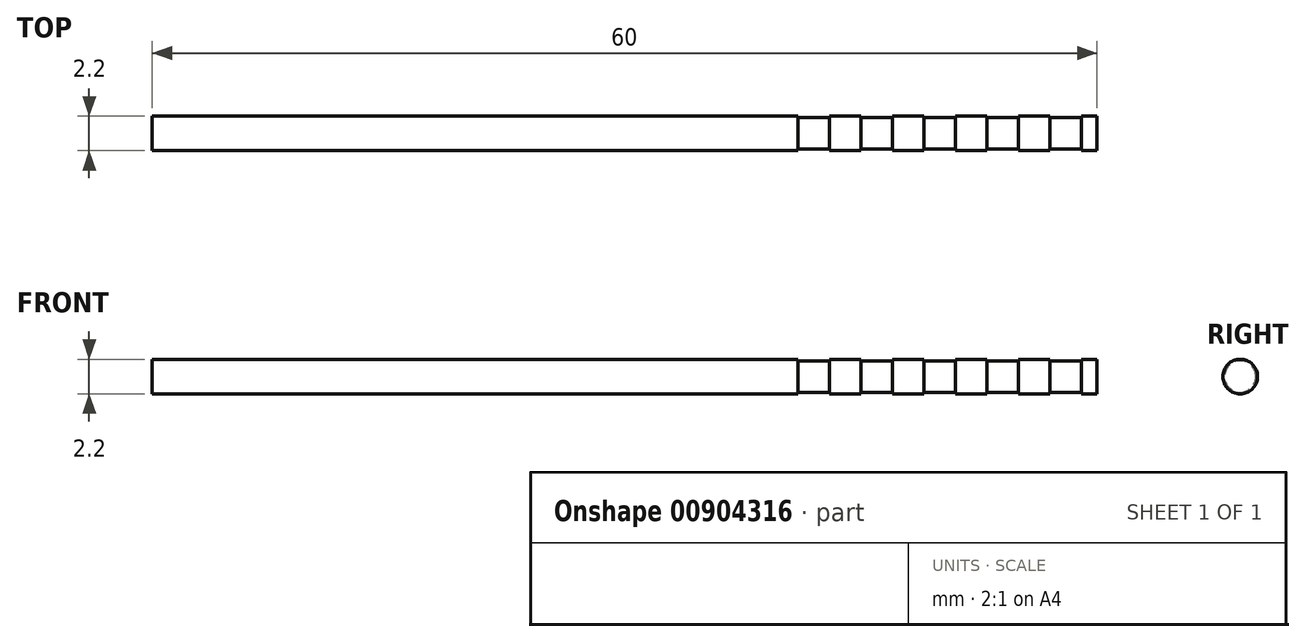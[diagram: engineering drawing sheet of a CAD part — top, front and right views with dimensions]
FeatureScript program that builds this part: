
annotation { "Feature Type Name" : "Feature", "Feature Type Description" : "" }
export const myFeature = defineFeature(function(context is Context, id is Id, definition is map)
    precondition{}
    {
        {
            var Q0;
            Q0=qCreatedBy(makeId("Front.planeOp"),FACE);
            var sketch = newSketch(context, id + "F0", { "sketchPlane" : qUnion([Q0])});
            skLineSegment(sketch, "E0.bottom", {"start": v(0, 0) * mm, "end": v(-25, 0) * mm});
            skLineSegment(sketch, "E0.top", {"start": v(0, 1.1) * mm, "end": v(-25, 1.1) * mm});
            skLineSegment(sketch, "E0.left", {"start": v(0, 0) * mm, "end": v(0, 1.1) * mm});
            skLineSegment(sketch, "E0.right", {"start": v(-25, 0) * mm, "end": v(-25, 1.1) * mm});
            skLineSegment(sketch, "E1.top", {"start": v(0, 1) * mm, "end": v(-25, 1) * mm});
            skLineSegment(sketch, "E1.left", {"start": v(0, 0) * mm, "end": v(0, 1) * mm});
            skLineSegment(sketch, "E1.right", {"start": v(-25, 0) * mm, "end": v(-25, 1) * mm});
            skLineSegment(sketch, "E2", {"start": v(-1, 1.1) * mm, "end": v(-1, 0) * mm});
            skLineSegment(sketch, "E3", {"start": v(-3, 1.1) * mm, "end": v(-3, 0) * mm});
            skLineSegment(sketch, "E4", {"start": v(-5, 1.1) * mm, "end": v(-5, 0) * mm});
            skLineSegment(sketch, "E5", {"start": v(-7, 1.1) * mm, "end": v(-7, 0) * mm});
            skLineSegment(sketch, "E6", {"start": v(-9, 1.1) * mm, "end": v(-9, 0) * mm});
            skLineSegment(sketch, "E7", {"start": v(-11, 1.1) * mm, "end": v(-11, 0) * mm});
            skLineSegment(sketch, "E8", {"start": v(-13, 1.1) * mm, "end": v(-13, 0) * mm});
            skLineSegment(sketch, "E9", {"start": v(-15, 1.1) * mm, "end": v(-15, 0) * mm});
            skLineSegment(sketch, "E10", {"start": v(-17, 1.1) * mm, "end": v(-17, 0) * mm});
            skLineSegment(sketch, "E11", {"start": v(-19, 1.1) * mm, "end": v(-19, 0) * mm});
            skSolve(sketch);
        }
        {
            var Q0;
            {var subQ0=sQuery(id+"F0.wireOp",EDGE,"E0.right");Q0=makeQuery(id+"F0.imprint","IMPRINT",FACE,{"disambiguationData":[TD([[makeQuery(id+"F0.imprint","IMPRINT",EDGE,{"derivedFrom":subQ0}),-1.0]])]});}
            var Q1;
            {var subQ0=sQuery(id+"F0.wireOp",EDGE,"E1.right");Q1=makeQuery(id+"F0.imprint","IMPRINT",FACE,{"disambiguationData":[TD([[makeQuery(id+"F0.imprint","IMPRINT",EDGE,{"derivedFrom":subQ0}),-1.0]])]});}
            var Q2;
            {var subQ0=sQuery(id+"F0.wireOp",EDGE,"E7");var subQ1=sQuery(id+"F0.wireOp",EDGE,"E0.bottom");var subQ2=makeQuery(id+"F0.imprint","INTERSECT",VERTEX,{"derivedFrom":[subQ1,subQ0]});Q2=makeQuery(id+"F0.imprint","IMPRINT",FACE,{"disambiguationData":[TD([[makeQuery(id+"F0.imprint","IMPRINT",EDGE,{"disambiguationData":[TD([[subQ2,-1.0]])],"derivedFrom":subQ1}),-1.0]])]});}
            var Q3;
            {var subQ0=sQuery(id+"F0.wireOp",EDGE,"E7");var subQ1=sQuery(id+"F0.wireOp",EDGE,"E0.top");var subQ2=makeQuery(id+"F0.imprint","INTERSECT",VERTEX,{"derivedFrom":[subQ1,subQ0]});Q3=makeQuery(id+"F0.imprint","IMPRINT",FACE,{"disambiguationData":[TD([[makeQuery(id+"F0.imprint","IMPRINT",EDGE,{"disambiguationData":[TD([[subQ2,-1.0]])],"derivedFrom":subQ1}),1.0]])]});}
            var Q4;
            {var subQ0=sQuery(id+"F0.wireOp",EDGE,"E6");var subQ1=sQuery(id+"F0.wireOp",EDGE,"E0.bottom");var subQ2=makeQuery(id+"F0.imprint","INTERSECT",VERTEX,{"derivedFrom":[subQ1,subQ0]});Q4=makeQuery(id+"F0.imprint","IMPRINT",FACE,{"disambiguationData":[TD([[makeQuery(id+"F0.imprint","IMPRINT",EDGE,{"disambiguationData":[TD([[subQ2,-1.0]])],"derivedFrom":subQ1}),-1.0]])]});}
            var Q5;
            {var subQ0=sQuery(id+"F0.wireOp",EDGE,"E5");var subQ1=sQuery(id+"F0.wireOp",EDGE,"E0.bottom");var subQ2=makeQuery(id+"F0.imprint","INTERSECT",VERTEX,{"derivedFrom":[subQ1,subQ0]});Q5=makeQuery(id+"F0.imprint","IMPRINT",FACE,{"disambiguationData":[TD([[makeQuery(id+"F0.imprint","IMPRINT",EDGE,{"disambiguationData":[TD([[subQ2,-1.0]])],"derivedFrom":subQ1}),-1.0]])]});}
            var Q6;
            {var subQ0=sQuery(id+"F0.wireOp",EDGE,"E5");var subQ1=sQuery(id+"F0.wireOp",EDGE,"E0.top");var subQ2=makeQuery(id+"F0.imprint","INTERSECT",VERTEX,{"derivedFrom":[subQ1,subQ0]});Q6=makeQuery(id+"F0.imprint","IMPRINT",FACE,{"disambiguationData":[TD([[makeQuery(id+"F0.imprint","IMPRINT",EDGE,{"disambiguationData":[TD([[subQ2,-1.0]])],"derivedFrom":subQ1}),1.0]])]});}
            var Q7;
            {var subQ0=sQuery(id+"F0.wireOp",EDGE,"E4");var subQ1=sQuery(id+"F0.wireOp",EDGE,"E0.bottom");var subQ2=makeQuery(id+"F0.imprint","INTERSECT",VERTEX,{"derivedFrom":[subQ1,subQ0]});Q7=makeQuery(id+"F0.imprint","IMPRINT",FACE,{"disambiguationData":[TD([[makeQuery(id+"F0.imprint","IMPRINT",EDGE,{"disambiguationData":[TD([[subQ2,-1.0]])],"derivedFrom":subQ1}),-1.0]])]});}
            var Q8;
            {var subQ0=sQuery(id+"F0.wireOp",EDGE,"E3");var subQ1=sQuery(id+"F0.wireOp",EDGE,"E0.bottom");var subQ2=makeQuery(id+"F0.imprint","INTERSECT",VERTEX,{"derivedFrom":[subQ1,subQ0]});Q8=makeQuery(id+"F0.imprint","IMPRINT",FACE,{"disambiguationData":[TD([[makeQuery(id+"F0.imprint","IMPRINT",EDGE,{"disambiguationData":[TD([[subQ2,-1.0]])],"derivedFrom":subQ1}),-1.0]])]});}
            var Q9;
            {var subQ0=sQuery(id+"F0.wireOp",EDGE,"E3");var subQ1=sQuery(id+"F0.wireOp",EDGE,"E0.top");var subQ2=makeQuery(id+"F0.imprint","INTERSECT",VERTEX,{"derivedFrom":[subQ1,subQ0]});Q9=makeQuery(id+"F0.imprint","IMPRINT",FACE,{"disambiguationData":[TD([[makeQuery(id+"F0.imprint","IMPRINT",EDGE,{"disambiguationData":[TD([[subQ2,-1.0]])],"derivedFrom":subQ1}),1.0]])]});}
            var Q10;
            {var subQ0=sQuery(id+"F0.wireOp",EDGE,"E2");var subQ1=sQuery(id+"F0.wireOp",EDGE,"E0.bottom");var subQ2=makeQuery(id+"F0.imprint","INTERSECT",VERTEX,{"derivedFrom":[subQ1,subQ0]});Q10=makeQuery(id+"F0.imprint","IMPRINT",FACE,{"disambiguationData":[TD([[makeQuery(id+"F0.imprint","IMPRINT",EDGE,{"disambiguationData":[TD([[subQ2,-1.0]])],"derivedFrom":subQ1}),-1.0]])]});}
            var Q11;
            {var subQ0=sQuery(id+"F0.wireOp",EDGE,"E1.left");Q11=makeQuery(id+"F0.imprint","IMPRINT",FACE,{"disambiguationData":[TD([[makeQuery(id+"F0.imprint","IMPRINT",EDGE,{"derivedFrom":subQ0}),1.0]])]});}
            var Q12;
            {var subQ0=sQuery(id+"F0.wireOp",EDGE,"E0.left");Q12=makeQuery(id+"F0.imprint","IMPRINT",FACE,{"disambiguationData":[TD([[makeQuery(id+"F0.imprint","IMPRINT",EDGE,{"derivedFrom":subQ0}),1.0]])]});}
            var Q13;
            {var subQ0=sQuery(id+"F0.wireOp",EDGE,"E8");var subQ1=sQuery(id+"F0.wireOp",EDGE,"E0.bottom");var subQ2=makeQuery(id+"F0.imprint","INTERSECT",VERTEX,{"derivedFrom":[subQ1,subQ0]});Q13=makeQuery(id+"F0.imprint","IMPRINT",FACE,{"disambiguationData":[TD([[makeQuery(id+"F0.imprint","IMPRINT",EDGE,{"disambiguationData":[TD([[subQ2,-1.0]])],"derivedFrom":subQ1}),-1.0]])]});}
            var Q14;
            {var subQ0=sQuery(id+"F0.wireOp",EDGE,"E9");var subQ1=sQuery(id+"F0.wireOp",EDGE,"E0.bottom");var subQ2=makeQuery(id+"F0.imprint","INTERSECT",VERTEX,{"derivedFrom":[subQ1,subQ0]});Q14=makeQuery(id+"F0.imprint","IMPRINT",FACE,{"disambiguationData":[TD([[makeQuery(id+"F0.imprint","IMPRINT",EDGE,{"disambiguationData":[TD([[subQ2,-1.0]])],"derivedFrom":subQ1}),-1.0]])]});}
            var Q15;
            {var subQ0=sQuery(id+"F0.wireOp",EDGE,"E9");var subQ1=sQuery(id+"F0.wireOp",EDGE,"E0.top");var subQ2=makeQuery(id+"F0.imprint","INTERSECT",VERTEX,{"derivedFrom":[subQ1,subQ0]});Q15=makeQuery(id+"F0.imprint","IMPRINT",FACE,{"disambiguationData":[TD([[makeQuery(id+"F0.imprint","IMPRINT",EDGE,{"disambiguationData":[TD([[subQ2,-1.0]])],"derivedFrom":subQ1}),1.0]])]});}
            var Q16;
            {var subQ0=sQuery(id+"F0.wireOp",EDGE,"E10");var subQ1=sQuery(id+"F0.wireOp",EDGE,"E0.bottom");var subQ2=makeQuery(id+"F0.imprint","INTERSECT",VERTEX,{"derivedFrom":[subQ1,subQ0]});Q16=makeQuery(id+"F0.imprint","IMPRINT",FACE,{"disambiguationData":[TD([[makeQuery(id+"F0.imprint","IMPRINT",EDGE,{"disambiguationData":[TD([[subQ2,-1.0]])],"derivedFrom":subQ1}),-1.0]])]});}
            var Q17;
            Q17=sQuery(id+"F0.wireOp",EDGE,"E0.bottom");
            revolve(context, id + "F1", {"surfaceOperationType" : NewSurfaceOperationType.NEW, "entities" : qUnion([Q0, Q1, Q2, Q3, Q4, Q5, Q6, Q7, Q8, Q9, Q10, Q11, Q12, Q13, Q14, Q15, Q16]), "axis" : qUnion([Q17]), "revolveType" : RevolveType.FULL});
        }
        {
            var Q0;
            Q0=makeQuery(id+"F1.opRevolve","SWEPT_FACE",FACE,{"disambiguationData":[OSD([sQuery(id+"F0.wireOp",EDGE,"E0.right"),sQuery(id+"F0.wireOp",EDGE,"E1.right")])]});
            extrude(context, id + "F2", {"entities" : qUnion([Q0]), "operationType" : NewBodyOperationType.ADD, "depth" : 10 * mm, "offsetDistance" : 25 * mm});
        }
        {
            var Q0;
            Q0=makeQuery(id+"F2.opExtrude","CAP_FACE",FACE,{"disambiguationData":[OSD([sQuery(id+"F0.wireOp",EDGE,"E0.right"),sQuery(id+"F0.wireOp",EDGE,"E1.right")])],"isStart":false});
            extrude(context, id + "F3", {"entities" : qUnion([Q0]), "operationType" : NewBodyOperationType.ADD, "depth" : 10 * mm, "offsetDistance" : 25 * mm});
        }
        {
            var Q0;
            Q0=makeQuery(id+"F3.opExtrude","CAP_FACE",FACE,{"disambiguationData":[OSD([sQuery(id+"F0.wireOp",EDGE,"E0.right"),sQuery(id+"F0.wireOp",EDGE,"E1.right")])],"isStart":false});
            extrude(context, id + "F4", {"entities" : qUnion([Q0]), "operationType" : NewBodyOperationType.ADD, "depth" : 15 * mm, "offsetDistance" : 25 * mm});
        }
    });
